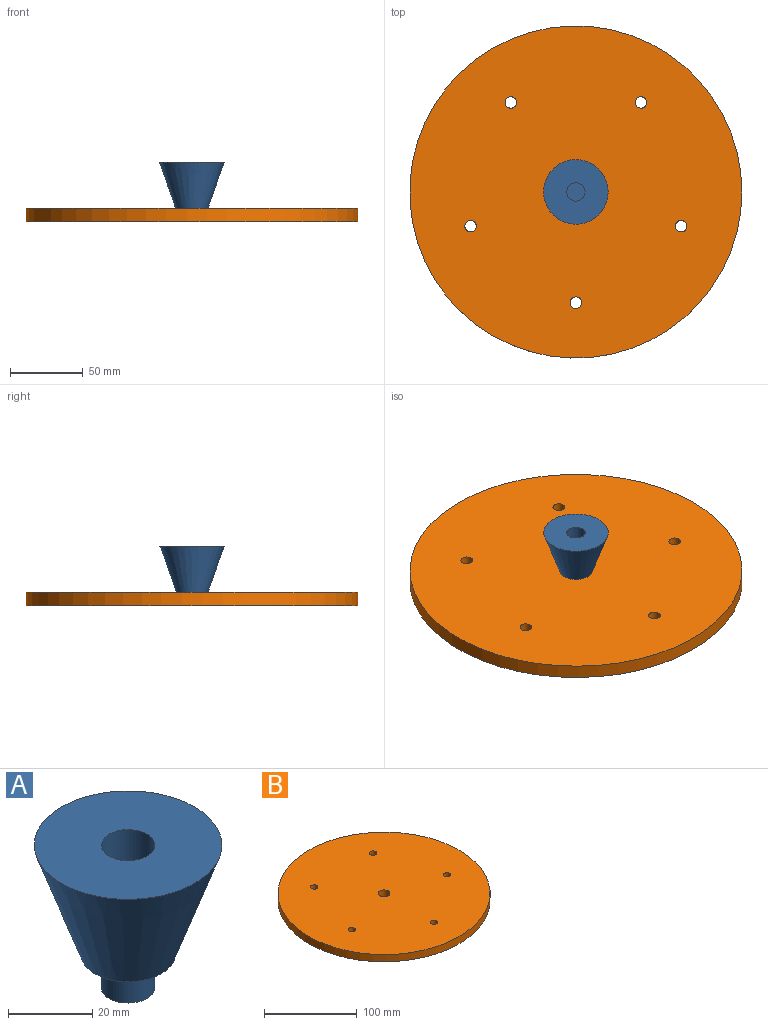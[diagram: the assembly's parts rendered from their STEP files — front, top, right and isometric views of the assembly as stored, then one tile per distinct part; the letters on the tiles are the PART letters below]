
ASSEMBLY  parts=2 mates=1
PART A: 7 faces, bbox 44.5x44.5x41.3 mm
  f0: plane 12.7x12.7mm, normal (0,0,-1), area 126.7mm2, adj f6
  f1: plane 12.7x12.7mm, normal (0,0,1), area 126.7mm2, adj f2
  f2: cylinder r=6.35mm len=19.05mm, axis (0,0,1), area 760.1mm2, adj f1,f3
  f3: plane 44.45x44.45mm, normal (0,0,1), area 1425.1mm2, adj f2,f4
  f4: cone r=11.11mm half-angle=19.3deg, axis (0,0,1), area 3523.1mm2, adj f3,f5
  f5: plane 22.23x22.23mm, normal (0,0,-1), area 261.3mm2, adj f4,f6
  f6: cylinder r=6.35mm len=12.7mm, axis (0,0,1), area 380mm2, adj f0,f5
PART B: 9 faces, bbox 228.6x228.6x9.5 mm
  f0: cylinder r=3.97mm len=9.53mm, axis (0,0,-1), area 237.5mm2, adj f6,f7
  f1: cylinder r=3.97mm len=9.53mm, axis (0,0,-1), area 237.5mm2, adj f6,f7
  f2: cylinder r=3.97mm len=9.53mm, axis (0,0,-1), area 237.5mm2, adj f6,f7
  f3: cylinder r=3.97mm len=9.53mm, axis (0,0,-1), area 237.5mm2, adj f6,f7
  f4: cylinder r=3.97mm len=9.53mm, axis (0,0,-1), area 237.5mm2, adj f6,f7
  f5: cylinder r=114.3mm len=228.6mm, axis (0,0,-1), area 6840.6mm2, adj f6,f7
  f6: plane 228.6x228.6mm, normal (0,0,1), area 40669.2mm2, adj f0,f1,f2,f3,f4,f5,f8
  f7: plane 228.6x228.6mm, normal (0,0,-1), area 40669.2mm2, adj f0,f1,f2,f3,f4,f5,f8
  f8: cylinder r=6.35mm len=12.7mm, axis (0,0,1), area 380mm2, adj f6,f7
PLACE A at identity
PLACE B at identity fixed
MATE fastened A.f2 <-> B.f5  axis (0,0,-1) through (0,0,0)mm
